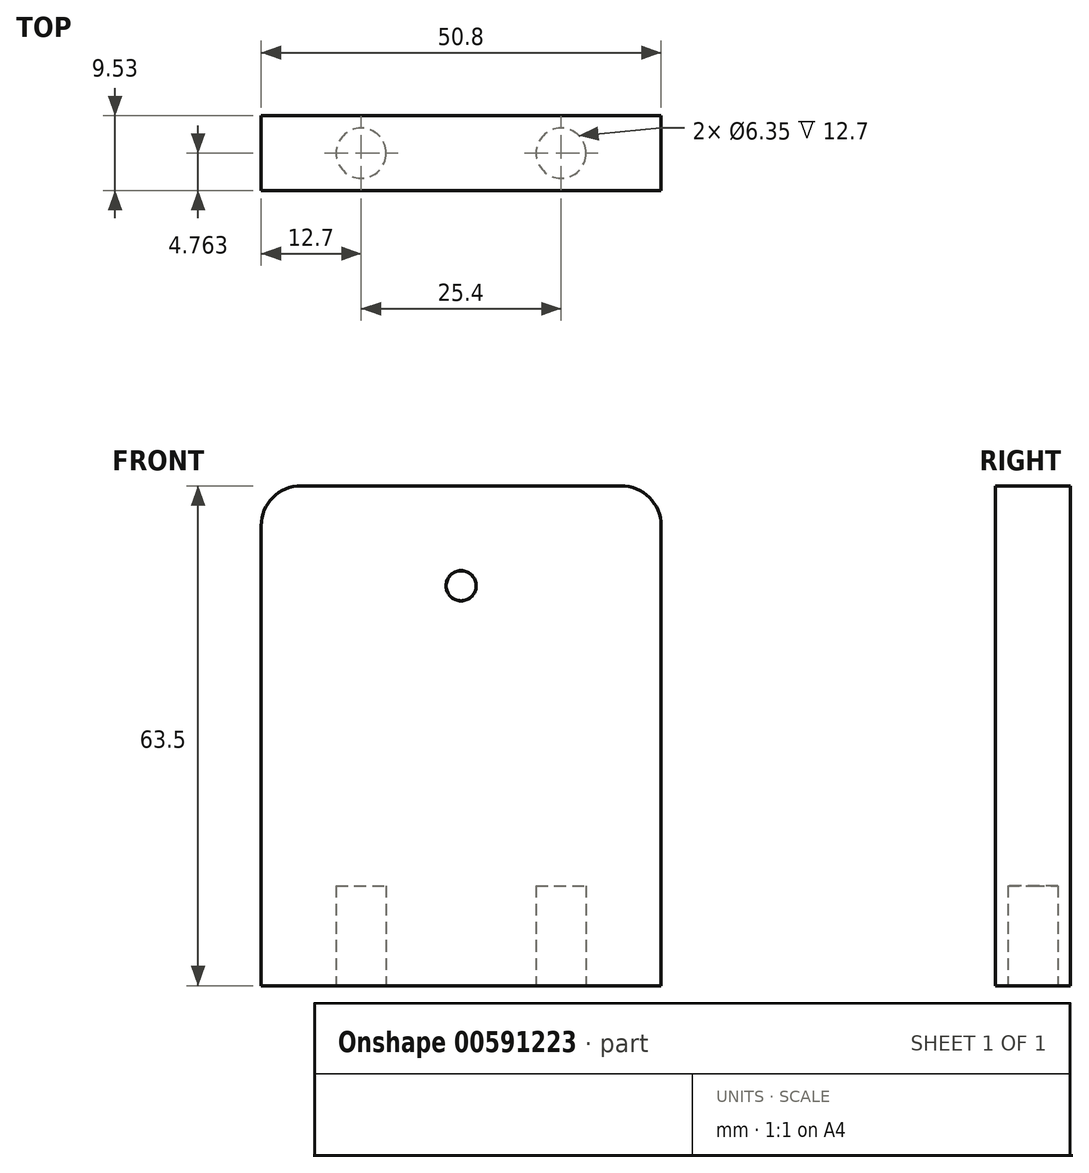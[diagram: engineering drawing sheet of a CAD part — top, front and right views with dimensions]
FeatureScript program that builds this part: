
annotation { "Feature Type Name" : "Feature", "Feature Type Description" : "" }
export const myFeature = defineFeature(function(context is Context, id is Id, definition is map)
    precondition{}
    {
        {
            var Q0;
            Q0=qCreatedBy(makeId("Top.planeOp"),FACE);
            var sketch = newSketch(context, id + "F0", { "sketchPlane" : qUnion([Q0])});
            skLineSegment(sketch, "E0.bottom", {"start": v(0, 0) * mm, "end": v(-50.8, 0) * mm});
            skLineSegment(sketch, "E0.top", {"start": v(0, 9.53) * mm, "end": v(-50.8, 9.52) * mm});
            skLineSegment(sketch, "E0.left", {"start": v(0, 0) * mm, "end": v(0, 9.53) * mm});
            skLineSegment(sketch, "E0.right", {"start": v(-50.8, 0) * mm, "end": v(-50.8, 9.52) * mm});
            skSolve(sketch);
        }
        {
            var Q0;
            Q0 = qSketchRegion(id + "F0", true);
            extrude(context, id + "F1", {"entities" : qUnion([Q0]), "depth" : 63.5 * mm, "offsetDistance" : 25.4 * mm});
        }
        {
            var Q0;
            Q0=makeQuery(id+"F1.opExtrude","SWEPT_FACE",FACE,{"disambiguationData":[OSD([sQuery(id+"F0.wireOp",EDGE,"E0.bottom")])]});
            var sketch = newSketch(context, id + "F2", { "sketchPlane" : qUnion([Q0])});
            skCircle(sketch, "E1", {"center": v(-25.4, 50.8) * mm, "radius": 3.18 * mm});
            skSolve(sketch);
        }
        {
            var Q0;
            Q0=makeQuery(id+"F2.imprint","IMPRINT",FACE,{"disambiguationData":[TD([[makeQuery(id+"F2.imprint","IMPRINT",EDGE,{"derivedFrom":sQuery(id+"F2.wireOp",EDGE,"E1")}),1.0]])]});
            extrude(context, id + "F3", {"entities" : qUnion([Q0]), "operationType" : NewBodyOperationType.REMOVE, "oppositeDirection" : true, "depth" : 3 / 203.2 * mm, "offsetDistance" : 25.4 * mm});
        }
        {
            var Q0;
            Q0=makeQuery(id+"F1.opExtrude","CAP_FACE",FACE,{"disambiguationData":[OSD([sQuery(id+"F0.wireOp",EDGE,"E0.bottom"),sQuery(id+"F0.wireOp",EDGE,"E0.top"),sQuery(id+"F0.wireOp",EDGE,"E0.left"),sQuery(id+"F0.wireOp",EDGE,"E0.right")])],"isStart":true});
            var sketch = newSketch(context, id + "F4", { "sketchPlane" : qUnion([Q0])});
            skCircle(sketch, "E2", {"center": v(-38.1, -4.76) * mm, "radius": 3.18 * mm});
            skCircle(sketch, "E3", {"center": v(-12.7, -4.76) * mm, "radius": 3.18 * mm});
            skSolve(sketch);
        }
        {
            var Q0;
            Q0 = qSketchRegion(id + "F4", true);
            extrude(context, id + "F5", {"entities" : qUnion([Q0]), "operationType" : NewBodyOperationType.REMOVE, "oppositeDirection" : true, "depth" : 12.7 * mm, "offsetDistance" : 25.4 * mm});
        }
        {
            var Q0;
            Q0=makeQuery(id+"F1.opExtrude","CAP_EDGE",EDGE,{"disambiguationData":[OSD([sQuery(id+"F0.wireOp",EDGE,"E0.right")])],"isStart":false});
            var Q1;
            Q1=makeQuery(id+"F1.opExtrude","CAP_EDGE",EDGE,{"disambiguationData":[OSD([sQuery(id+"F0.wireOp",EDGE,"E0.left")])],"isStart":false});
            fillet(context, id + "F6", {"entities" : qUnion([Q0, Q1]), "radius" : 5.08 * mm, "tangentPropagation" : true, "allowEdgeOverflow" : false});
        }
        {
            var Q0;
            Q0=makeQuery(id+"F3.boolean.opBoolean","COPY",EDGE,{"derivedFrom":makeQuery(id+"F3.opExtrude","CAP_EDGE",EDGE,{"disambiguationData":[OSD([sQuery(id+"F2.wireOp",EDGE,"E1")])],"isStart":true})});
            var Q1;
            Q1=makeQuery(id+"F3.boolean.opBoolean","COPY",EDGE,{"derivedFrom":makeQuery(id+"F3.opExtrude","CAP_EDGE",EDGE,{"disambiguationData":[OSD([sQuery(id+"F2.wireOp",EDGE,"E1")])],"isStart":false})});
            chamfer(context, id + "F7", {"entities" : qUnion([Q0, Q1]), "width" : 1.27 * mm, "tangentPropagation" : true});
        }
    });
